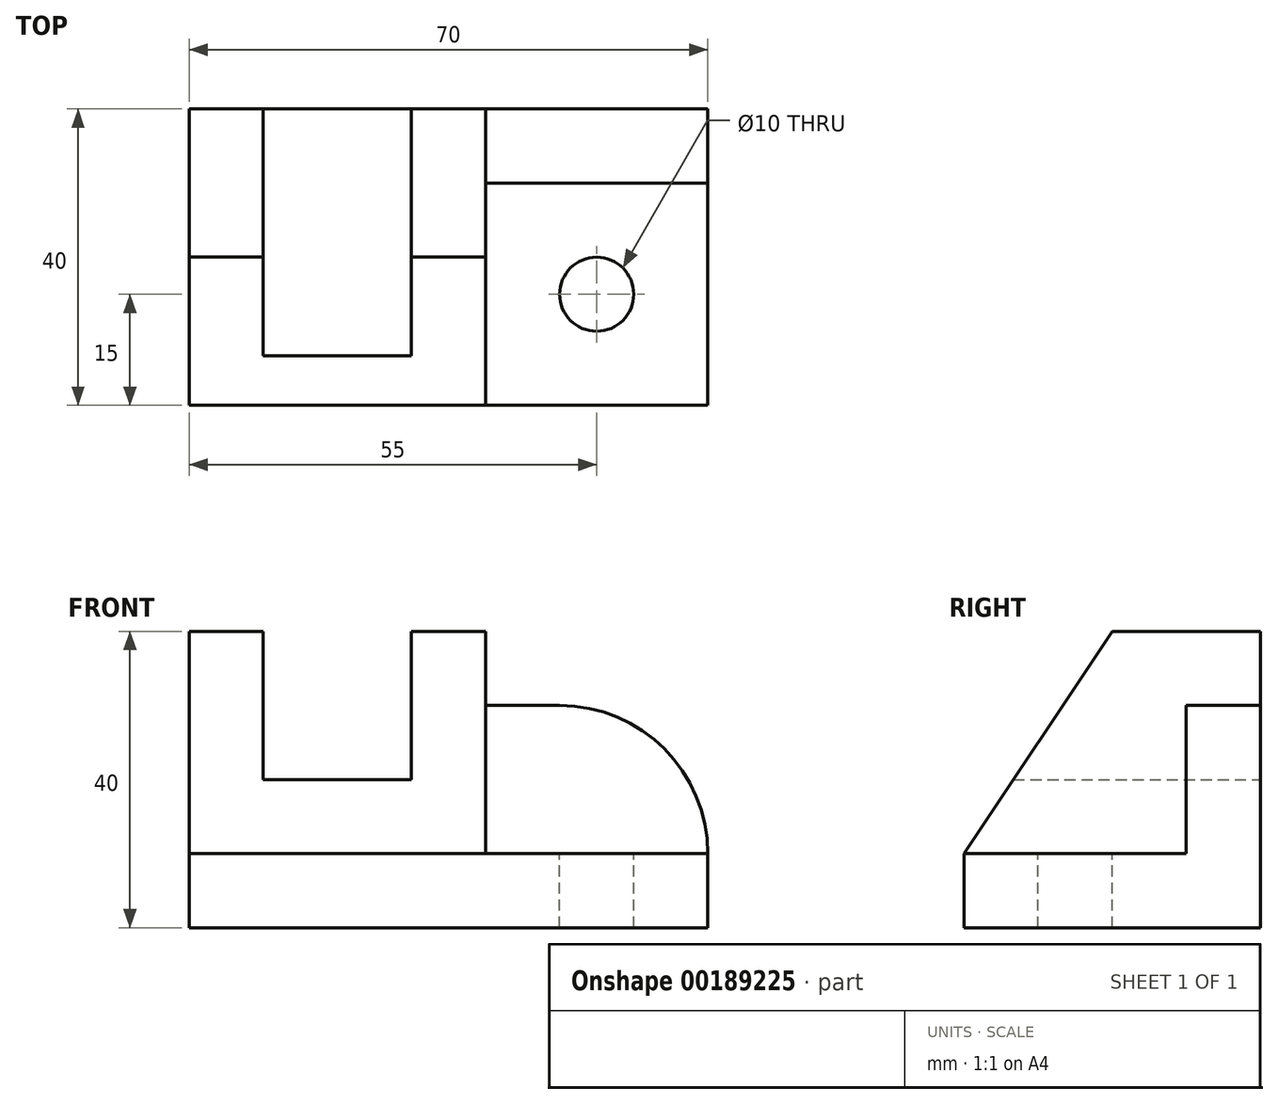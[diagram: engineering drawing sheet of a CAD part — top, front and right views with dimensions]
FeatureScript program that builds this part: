
annotation { "Feature Type Name" : "Feature", "Feature Type Description" : "" }
export const myFeature = defineFeature(function(context is Context, id is Id, definition is map)
    precondition{}
    {
        {
            var Q0;
            Q0=qCreatedBy(makeId("Front.planeOp"),FACE);
            var sketch = newSketch(context, id + "F0", { "sketchPlane" : qUnion([Q0])});
            skLineSegment(sketch, "E0", {"start": v(0, 0) * mm, "end": v(0, 40) * mm});
            skLineSegment(sketch, "E1", {"start": v(0, 40) * mm, "end": v(40, 40) * mm});
            skLineSegment(sketch, "E2", {"start": v(40, 40) * mm, "end": v(40, 10) * mm});
            skLineSegment(sketch, "E3", {"start": v(40, 10) * mm, "end": v(70, 10) * mm});
            skLineSegment(sketch, "E4", {"start": v(70, 10) * mm, "end": v(70, 0) * mm});
            skLineSegment(sketch, "E5", {"start": v(70, 0) * mm, "end": v(0, 0) * mm});
            skSolve(sketch);
        }
        {
            var Q0;
            Q0=makeQuery(id+"F0.imprint","IMPRINT",FACE,{"disambiguationData":[TD([[makeQuery(id+"F0.imprint","IMPRINT",EDGE,{"derivedFrom":sQuery(id+"F0.wireOp",EDGE,"E0")}),-1.0]])]});
            extrude(context, id + "F1", {"entities" : qUnion([Q0]), "endBound" : BoundingType.SYMMETRIC, "depth" : 40 * mm});
        }
        {
            var Q0;
            Q0=makeQuery(id+"F1.opExtrude","CAP_EDGE",EDGE,{"disambiguationData":[OSD([sQuery(id+"F0.wireOp",EDGE,"E1")])],"isStart":false});
            chamfer(context, id + "F2", {"entities" : qUnion([Q0]), "chamferType" : ChamferType.TWO_OFFSETS, "width1" : 20 * mm, "oppositeDirection" : false, "width2" : 30 * mm, "tangentPropagation" : true});
        }
        {
            var Q0;
            Q0=makeQuery(id+"F1.opExtrude","CAP_FACE",FACE,{"disambiguationData":[OSD([sQuery(id+"F0.wireOp",EDGE,"E0"),sQuery(id+"F0.wireOp",EDGE,"E1"),sQuery(id+"F0.wireOp",EDGE,"E2"),sQuery(id+"F0.wireOp",EDGE,"E3"),sQuery(id+"F0.wireOp",EDGE,"E4"),sQuery(id+"F0.wireOp",EDGE,"E5")])],"isStart":true});
            var sketch = newSketch(context, id + "F3", { "sketchPlane" : qUnion([Q0])});
            skLineSegment(sketch, "E6", {"start": v(-10, 40) * mm, "end": v(-10, 20) * mm});
            skPoint(sketch, "E6.endSnap0", {"position": v(0, 20) * mm});
            skLineSegment(sketch, "E7", {"start": v(-10, 20) * mm, "end": v(-30, 20) * mm});
            skLineSegment(sketch, "E8", {"start": v(-30, 20) * mm, "end": v(-30, 40) * mm});
            skLineSegment(sketch, "E9.0", {"start": v(-10, 40) * mm, "end": v(-30, 40) * mm});
            skPoint(sketch, "E10.orphan", {"position": v(0, 40) * mm});
            skPoint(sketch, "E11.orphan", {"position": v(-40, 40) * mm});
            skSolve(sketch);
        }
        {
            var Q0;
            Q0=makeQuery(id+"F3.imprint","IMPRINT",FACE,{"disambiguationData":[TD([[makeQuery(id+"F3.imprint","IMPRINT",EDGE,{"derivedFrom":sQuery(id+"F3.wireOp",EDGE,"E6")}),-1.0]])]});
            extrude(context, id + "F4", {"entities" : qUnion([Q0]), "operationType" : NewBodyOperationType.REMOVE, "endBound" : BoundingType.THROUGH_ALL, "oppositeDirection" : true, "depth" : 25 * mm});
        }
        {
            var Q0;
            Q0=makeQuery(id+"F1.opExtrude","CAP_FACE",FACE,{"disambiguationData":[OSD([sQuery(id+"F0.wireOp",EDGE,"E0"),sQuery(id+"F0.wireOp",EDGE,"E1"),sQuery(id+"F0.wireOp",EDGE,"E2"),sQuery(id+"F0.wireOp",EDGE,"E3"),sQuery(id+"F0.wireOp",EDGE,"E4"),sQuery(id+"F0.wireOp",EDGE,"E5")])],"isStart":true});
            var sketch = newSketch(context, id + "F5", { "sketchPlane" : qUnion([Q0])});
            skLineSegment(sketch, "E12", {"start": v(-40, 30) * mm, "end": v(-50, 30) * mm});
            skArc(sketch, "E13", {"start": v(-50, 30) * mm, "mid": v(-64.14, 24.14) * mm, "end": v(-70, 10) * mm});
            skLineSegment(sketch, "E14.0", {"start": v(-40, 30) * mm, "end": v(-40, 10) * mm});
            skLineSegment(sketch, "E15.0", {"start": v(-40, 10) * mm, "end": v(-70, 10) * mm});
            skPoint(sketch, "E16.orphan", {"position": v(-40, 40) * mm});
            skSolve(sketch);
        }
        {
            var Q0;
            Q0=makeQuery(id+"F5.imprint","IMPRINT",FACE,{"disambiguationData":[TD([[makeQuery(id+"F5.imprint","IMPRINT",EDGE,{"derivedFrom":sQuery(id+"F5.wireOp",EDGE,"E12")}),1.0]])]});
            extrude(context, id + "F6", {"entities" : qUnion([Q0]), "operationType" : NewBodyOperationType.ADD, "oppositeDirection" : true, "depth" : 10 * mm});
        }
        {
            var Q0;
            Q0=makeQuery(id+"F1.opExtrude","SWEPT_FACE",FACE,{"disambiguationData":[OSD([sQuery(id+"F0.wireOp",EDGE,"E3")])]});
            var sketch = newSketch(context, id + "F7", { "sketchPlane" : qUnion([Q0])});
            skCircle(sketch, "E17", {"center": v(55, -5) * mm, "radius": 5 * mm});
            skSolve(sketch);
        }
        {
            var Q0;
            Q0=makeQuery(id+"F7.imprint","IMPRINT",FACE,{"disambiguationData":[TD([[makeQuery(id+"F7.imprint","IMPRINT",EDGE,{"derivedFrom":sQuery(id+"F7.wireOp",EDGE,"E17")}),1.0]])]});
            extrude(context, id + "F8", {"entities" : qUnion([Q0]), "operationType" : NewBodyOperationType.REMOVE, "endBound" : BoundingType.UP_TO_NEXT, "oppositeDirection" : true, "depth" : 25 * mm});
        }
    });
